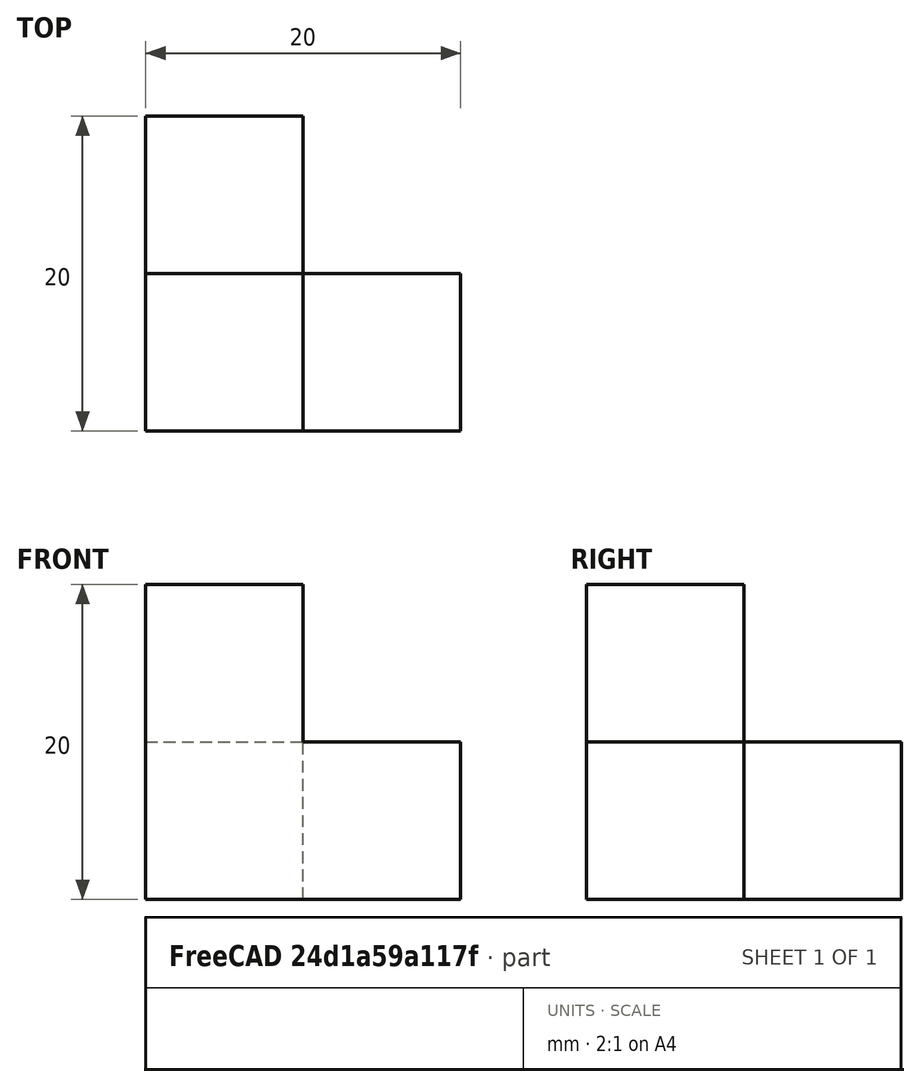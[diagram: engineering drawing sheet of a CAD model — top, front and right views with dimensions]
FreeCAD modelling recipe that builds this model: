
FCSTD DOCUMENT  (FreeCAD 1.0R39319 (Git))
Label: ojt1_t04p01_refine shape
License: All rights reserved
LicenseURL: https://en.wikipedia.org/wiki/All_rights_reserved
objects: Part::Box×4, Part::MultiFuse×1
note: 5 computed .brp shape members not serialized (recipe doc carries the construction recipe); baked Part::Feature solids carry a one-line shape summary decoded from their .brp

FEATURE [Part::Box] Box  label="Cub"
  AttacherType = Attacher::AttachEngine3D
  Height = 10
  Length = 10
  Width = 10
FEATURE [Part::Box] Box001  label="Cub001"
  AttacherType = Attacher::AttachEngine3D
  Height = 10
  Length = 10
  Placement = pos=(0,0,10) rot=(0,0,1;0rad)
  Width = 10
FEATURE [Part::Box] Box003  label="Cub003"
  AttacherType = Attacher::AttachEngine3D
  Height = 10
  Length = 10
  Placement = pos=(0,10,0) rot=(0,0,1;0rad)
  Width = 10
FEATURE [Part::Box] Box004  label="Cub004"
  AttacherType = Attacher::AttachEngine3D
  Height = 10
  Length = 10
  Placement = pos=(10,0,0) rot=(0,0,1;0rad)
  Width = 10
FEATURE [Part::MultiFuse] Fusion
  Refine = true
  Shapes = -> [Box,Box001,Box003,Box004]
